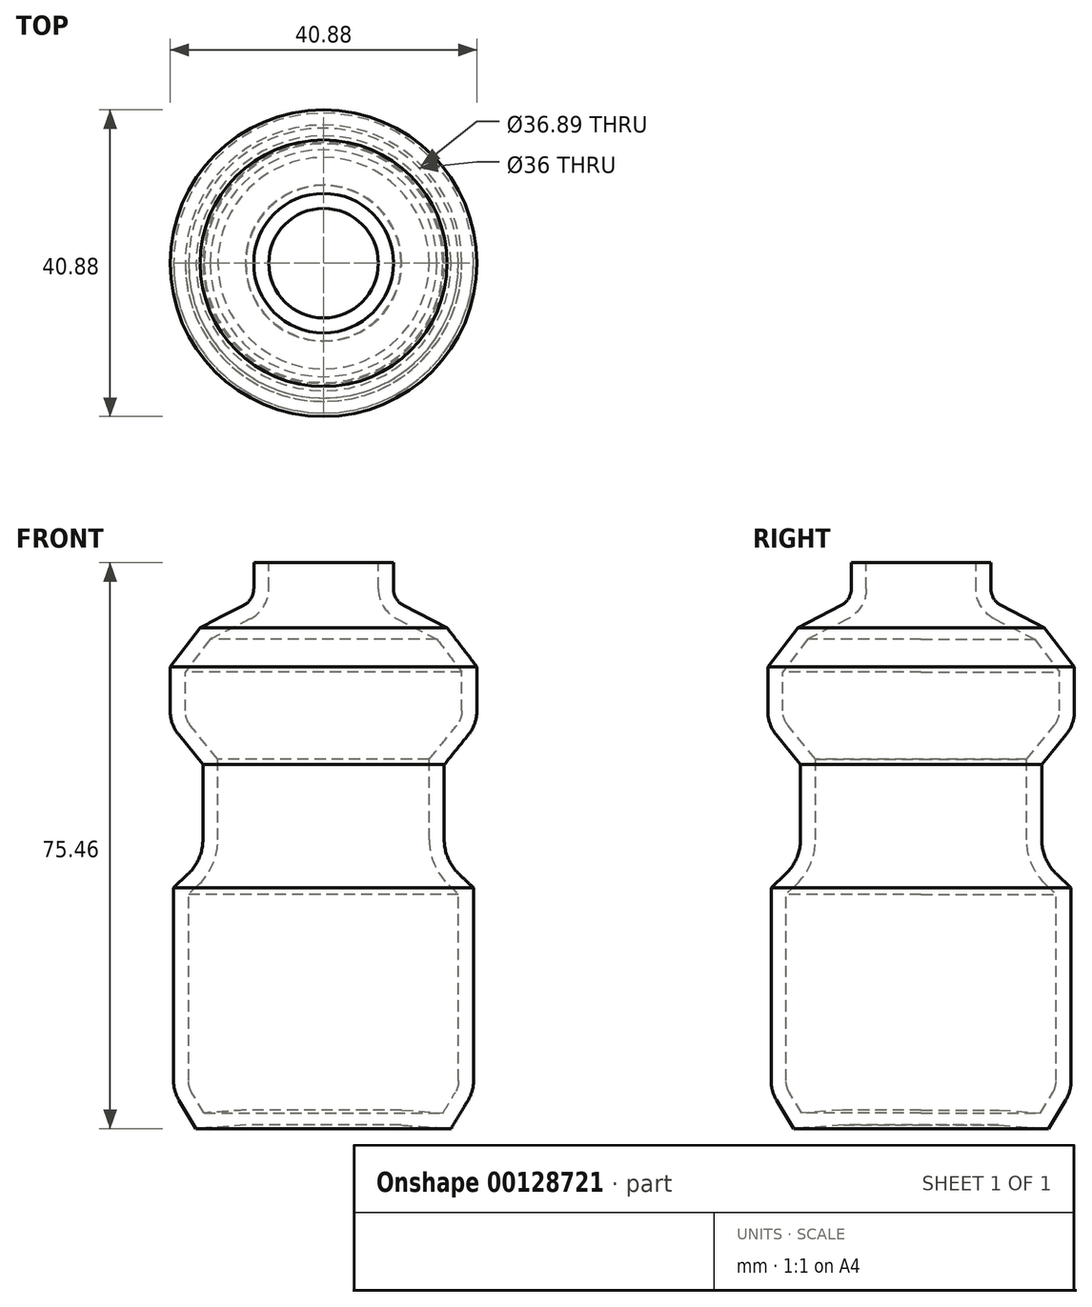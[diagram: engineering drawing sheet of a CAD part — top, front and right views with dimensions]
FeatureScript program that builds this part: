
annotation { "Feature Type Name" : "Feature", "Feature Type Description" : "" }
export const myFeature = defineFeature(function(context is Context, id is Id, definition is map)
    precondition{}
    {
        {
            var Q0;
            Q0=qCreatedBy(makeId("Front.planeOp"),FACE);
            var sketch = newSketch(context, id + "F0", { "sketchPlane" : qUnion([Q0])});
            skLineSegment(sketch, "E0", {"start": v(0, 0) * mm, "end": v(10.35, 0) * mm});
            skLineSegment(sketch, "E1", {"start": v(10.35, 0) * mm, "end": v(17, -0.46) * mm});
            skLineSegment(sketch, "E2", {"start": v(17, -0.46) * mm, "end": v(20, 4.54) * mm});
            skLineSegment(sketch, "E3", {"start": v(20, 4.54) * mm, "end": v(20, 31.63) * mm});
            skLineSegment(sketch, "E4", {"start": v(20, 31.63) * mm, "end": v(18.07, 33.47) * mm});
            skLineSegment(sketch, "E5", {"start": v(16.1, 38.07) * mm, "end": v(16.1, 48.07) * mm});
            skLineSegment(sketch, "E6", {"start": v(16.1, 48.07) * mm, "end": v(20.44, 53.46) * mm});
            skLineSegment(sketch, "E7", {"start": v(20.44, 53.46) * mm, "end": v(20.44, 61.12) * mm});
            skLineSegment(sketch, "E8", {"start": v(20.44, 61.12) * mm, "end": v(16.44, 66.34) * mm});
            skLineSegment(sketch, "E9", {"start": v(16.44, 66.34) * mm, "end": v(9.3, 70) * mm});
            skLineSegment(sketch, "E10", {"start": v(9.3, 70) * mm, "end": v(9.3, 75) * mm});
            skLineSegment(sketch, "E11", {"start": v(9.3, 75) * mm, "end": v(0, 75) * mm});
            skLineSegment(sketch, "E12", {"start": v(0, 75) * mm, "end": v(0, 0) * mm});
            skPoint(sketch, "E13.visualSharp", {"position": v(16.1, 35.35) * mm});
            skArc(sketch, "E13.filletArc", {"start": v(16.1, 38.07) * mm, "mid": v(16.6, 35.57) * mm, "end": v(18.07, 33.47) * mm});
            skSolve(sketch);
        }
        {
            var Q0;
            Q0 = qSketchRegion(id + "F0", true);
            var Q1;
            Q1=sQuery(id+"F0.wireOp",EDGE,"E12");
            revolve(context, id + "F1", {"entities" : qUnion([Q0]), "axis" : qUnion([Q1]), "revolveType" : RevolveType.FULL});
        }
        {
            var Q0;
            Q0=makeQuery(id+"F1.opRevolve","SWEPT_EDGE",EDGE,{"disambiguationData":[OSD([sQuery(id+"F0.wireOp",EDGE,"E2"),sQuery(id+"F0.wireOp",EDGE,"E3")])]});
            fillet(context, id + "F2", {"entities" : qUnion([Q0]), "radius" : 5.08 * mm, "tangentPropagation" : true, "allowEdgeOverflow" : false});
        }
        {
            var Q0;
            Q0=makeQuery(id+"F1.opRevolve","SWEPT_EDGE",EDGE,{"disambiguationData":[OSD([sQuery(id+"F0.wireOp",EDGE,"E6"),sQuery(id+"F0.wireOp",EDGE,"E7")])]});
            fillet(context, id + "F3", {"entities" : qUnion([Q0]), "radius" : 5.08 * mm, "tangentPropagation" : true, "allowEdgeOverflow" : false});
        }
        {
            var Q0;
            Q0=makeQuery(id+"F1.opRevolve","SWEPT_EDGE",EDGE,{"disambiguationData":[OSD([sQuery(id+"F0.wireOp",EDGE,"E9"),sQuery(id+"F0.wireOp",EDGE,"E10")])]});
            fillet(context, id + "F4", {"entities" : qUnion([Q0]), "radius" : 2.54 * mm, "tangentPropagation" : true, "allowEdgeOverflow" : false});
        }
        {
            var Q0;
            Q0=makeQuery(id+"F1.opRevolve","SWEPT_FACE",FACE,{"disambiguationData":[OSD([sQuery(id+"F0.wireOp",EDGE,"E11")])]});
            shell(context, id + "F5", {"entities" : qUnion([Q0]), "thickness" : 2 * mm});
        }
    });
